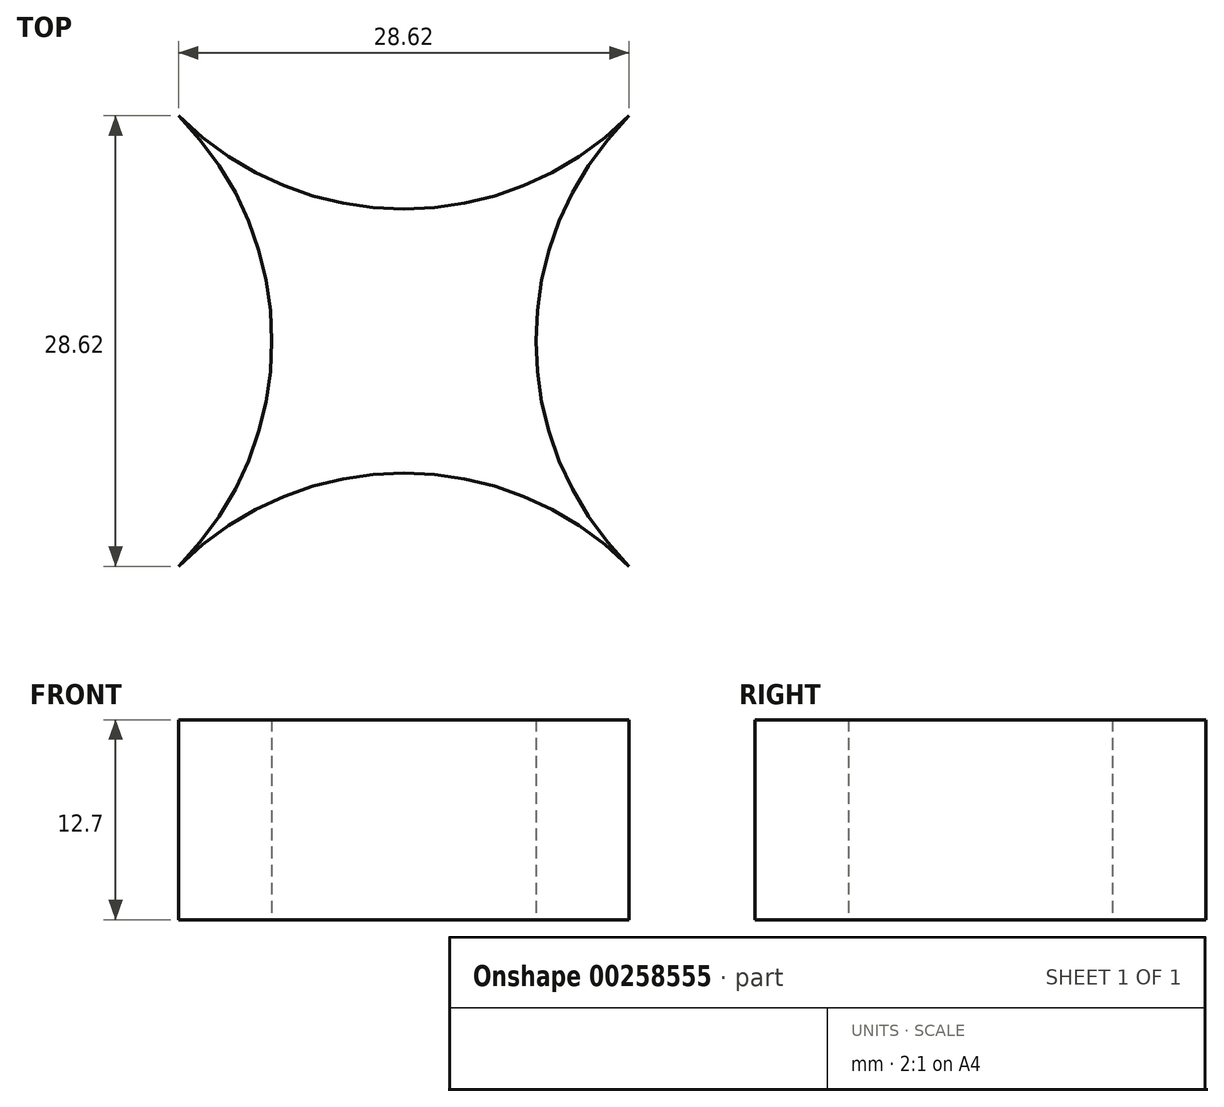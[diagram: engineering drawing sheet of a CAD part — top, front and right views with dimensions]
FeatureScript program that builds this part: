
annotation { "Feature Type Name" : "Feature", "Feature Type Description" : "" }
export const myFeature = defineFeature(function(context is Context, id is Id, definition is map)
    precondition{}
    {
        {
            var Q0;
            Q0=qCreatedBy(makeId("Top.planeOp"),FACE);
            var sketch = newSketch(context, id + "F0", { "sketchPlane" : qUnion([Q0])});
            skCircle(sketch, "E0", {"center": v(28.62, 0) * mm, "radius": 16.27 * mm});
            skCircle(sketch, "E1", {"center": v(28.62, 0) * mm, "radius": 20.24 * mm});
            skCircle(sketch, "E2", {"center": v(0, 28.62) * mm, "radius": 16.27 * mm});
            skCircle(sketch, "E3", {"center": v(0, 28.62) * mm, "radius": 20.24 * mm});
            skCircle(sketch, "E4", {"center": v(-28.62, 0) * mm, "radius": 16.27 * mm});
            skCircle(sketch, "E5", {"center": v(-28.62, 0) * mm, "radius": 20.24 * mm});
            skCircle(sketch, "E6", {"center": v(0, -28.62) * mm, "radius": 20.24 * mm});
            skCircle(sketch, "E7", {"center": v(0, -28.62) * mm, "radius": 16.27 * mm});
            skLineSegment(sketch, "E8", {"start": v(0, 0) * mm, "end": v(-28.62, 0) * mm, "construction": true});
            skLineSegment(sketch, "E9", {"start": v(0, 0) * mm, "end": v(28.62, 0) * mm, "construction": true});
            skLineSegment(sketch, "E10", {"start": v(0, 0) * mm, "end": v(0, 28.62) * mm, "construction": true});
            skLineSegment(sketch, "E11", {"start": v(0, 0) * mm, "end": v(0, -28.62) * mm, "construction": true});
            skLineSegment(sketch, "E12", {"start": v(0, 0) * mm, "end": v(-27.5, 0) * mm});
            skSolve(sketch);
        }
        {
            var Q0;
            {var subQ0=sQuery(id+"F0.wireOp",EDGE,"E3");var subQ1=sQuery(id+"F0.wireOp",EDGE,"E1");var subQ2=makeQuery(id+"F0.imprint","INTERSECT",VERTEX,{"derivedFrom":[subQ1,subQ0]});Q0=makeQuery(id+"F0.imprint","IMPRINT",FACE,{"disambiguationData":[TD([[makeQuery(id+"F0.imprint","IMPRINT",EDGE,{"disambiguationData":[TD([[subQ2,-1.0]])],"derivedFrom":subQ1}),-1.0]])]});}
            extrude(context, id + "F1", {"entities" : qUnion([Q0]), "depth" : 12.7 * mm});
        }
    });
